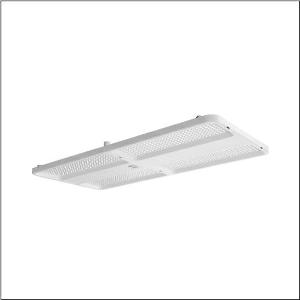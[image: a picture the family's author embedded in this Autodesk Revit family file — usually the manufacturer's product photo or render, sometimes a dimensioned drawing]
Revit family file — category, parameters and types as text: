
# Revit family: highbay_21_maxi_52hn11db4mda01
name_source: partatom
category: Lighting Fixtures
units: mm (PartAtom-declared; Revit-internal decimal feet)

## family parameters
Cut with Voids When Loaded = No
Host = Face
Light Source = No
Part Type = Normal
Room Calculation Point = No
Round Connector Dimension = Use Diameter
Shared = No

## types (1)
- --- (1 x LED, 28000 lm, 144.5 W, 4000K)
    Apparent Load = 144 VA
    CIE Flux Codes = 89 97 99 100 100
    Color Rendering = 80
    Color Temperature = 4000K
    Default Elevation = 1800 mm
    Description = high bay luminaire Highbay 21 maxi; direct symmetric narrow distribution, light control with lens of PMMA; UGR ≤ 19 (X = 4H | Y = 8H | S = 0.25H | reflection values 70/50/20); luminous flux: 28.000lm; light colour: 840, colour temperature: 4000K, MacAdam ≤ 3 SDCM (initial), colour rendering: CRI > 80; luminous efficacy: 193,8lm/W; rated service life: 75.000h (L80) at AT= ta max; control: Bluetooth Mesh; for wireless networking: Node multi-sensor luminaire for setting up a local control solution without a higher-level application controller, intelligence completely integrated into the luminaire; with auto-swarm function: leading lighting creates safety. The function is already active without any „out-of-the-box“ commissioning; commissioning is not necessary thanks to „out-of-the-box“ functions: basic functions (presence lighting, follow-up times, fading times, etc.) are already preset at the factory; no control line such as DALI between the Node multi-sensor luminaires and Nodes is required, wireless integration of other Node luminaires and Node multi-sensor luminaires into the network is possible; number of Node multi-sensor luminaires in the project can be expanded as required, network sizes > 300 Nodes can be realized; can also be connected to lighting or building automation via various gateways upon request; integrated DALI2 ECG provides luminaire data (according to IEC62386, Part 251), energy data (Part 252), and monitoring and analytics data (Part 253) to higher-level systems for further processing; luminaire with PIR sensor (passive-infrared); with light sensor; luminaire connection: terminal, 5-pole, max. 2.5mm² (cable entry for one cable, Ø 8.5..16mm); mains connection: 230..240V, AC 50/60Hz; connected load: 144,5W; protection rating (complete): IP65; insulation class (complete): insulation class I (protective earthing); protection symbol: D; certification: CE, UKCA; internal wiring halogen-free; luminaire LABS conformity tested according to VDMA 24364:2018-05; Suitable for use in the food industry according to the specifications of IFS-Food, HACCP and/or BRC; housing frame of high-performance plastic PA6, matt traffic white (RAL 9016); cover of PMMA; dimension (LxWxH): 946 x 442 x 72mm; permissible operating ambient temperature: -20..+45°C (reducing of maximum allowable ambient temperature of 5°C with ceiling mounting); packaging unit: 1 piece; (delivery without accessories; please order mounting accessories separately)
    Height = 72 mm  [stored 0.23622 ft]
    Lamp = 1 x LED
    Lamp Light Flux = 28000 lm
    Lamp Power = 144.5 W
    Lamp count = 1
    Length = 946 mm
    Luminous efficacy = 194 lm/W
    Manufacturer = Siteco
    ModVariant = No
    Model = 52HN11DB4MDA01
    Mounting Place = Ceiling
    Mounting Type = Pendant
    Number of Poles = 1
    OnlyDefault = Yes
    Power Factor = 1
    Product Name = Highbay 21 maxi
    Product group = high bay luminaire
    ProductGroupID = 902
    Protection Class = Protection class I
    Protection Degree = IP 65
    RLX_Detail_Level = 1
    RLX_Emergency_Light_Flux = 0 lm
    RLX_Emergency_Type = 0
    RLX_Emergency_Type_DB = No
    RlxData = <blob elided: 128629 chars, md5=d9d79246>
    Socket = socket
    Standby Power = 0 W
    System Light Flux = 28000 lm
    System Power = 144 W
    Type Comments = factory setting: luminous flux: 100 % | dim-lin: 254 | 668 mA
    Type Image = l_1363267.jpg
    URL = http://relux.com
    VarID = @adj_012785
    Voltage = 0 V
    Weight = 0.00 kg
    Width = 442 mm

note: [stored X ft] marks values corroborated as IEEE doubles in the binary element streams (Revit-internal decimal feet)

## geometry (parser evidence)
native form markers: Blend x4, Sweep x9
no freeform markers — native parametric forms only
